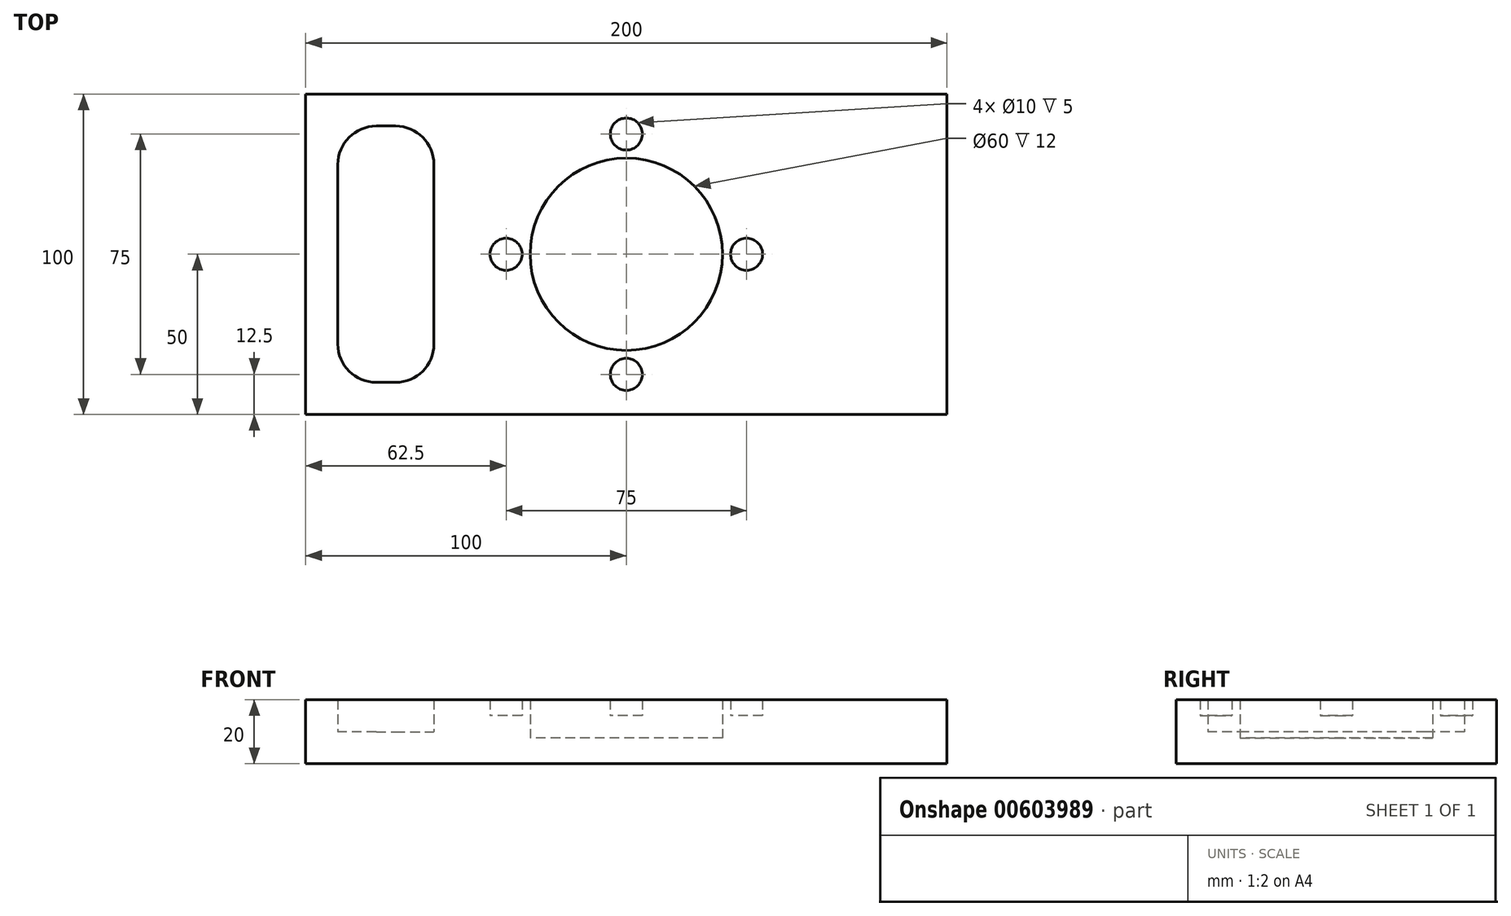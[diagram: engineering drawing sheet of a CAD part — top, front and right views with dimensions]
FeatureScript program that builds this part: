
annotation { "Feature Type Name" : "Feature", "Feature Type Description" : "" }
export const myFeature = defineFeature(function(context is Context, id is Id, definition is map)
    precondition{}
    {
        {
            var Q0;
            Q0=qCreatedBy(makeId("Top.planeOp"),FACE);
            var sketch = newSketch(context, id + "F0", { "sketchPlane" : qUnion([Q0])});
            skLineSegment(sketch, "E0.bottom", {"start": v(-100, 50) * mm, "end": v(100, 50) * mm});
            skLineSegment(sketch, "E0.top", {"start": v(-100, -50) * mm, "end": v(100, -50) * mm});
            skLineSegment(sketch, "E0.left", {"start": v(-100, 50) * mm, "end": v(-100, -50) * mm});
            skLineSegment(sketch, "E0.right", {"start": v(100, 50) * mm, "end": v(100, -50) * mm});
            skPoint(sketch, "E0.middle", {"position": v(0, 0) * mm});
            skSolve(sketch);
        }
        {
            var Q0;
            Q0=makeQuery(id+"F0.imprint","IMPRINT",FACE,{"disambiguationData":[TD([[makeQuery(id+"F0.imprint","IMPRINT",EDGE,{"derivedFrom":sQuery(id+"F0.wireOp",EDGE,"E0.bottom")}),-1.0]])]});
            extrude(context, id + "F1", {"entities" : qUnion([Q0]), "depth" : 8 * mm, "offsetDistance" : 25 * mm});
        }
        {
            var Q0;
            Q0=makeQuery(id+"F1.opExtrude","CAP_FACE",FACE,{"disambiguationData":[OSD([sQuery(id+"F0.wireOp",EDGE,"E0.bottom"),sQuery(id+"F0.wireOp",EDGE,"E0.top"),sQuery(id+"F0.wireOp",EDGE,"E0.left"),sQuery(id+"F0.wireOp",EDGE,"E0.right")])],"isStart":false});
            var sketch = newSketch(context, id + "F2", { "sketchPlane" : qUnion([Q0])});
            skLineSegment(sketch, "E1.bottom", {"start": v(-100, 50) * mm, "end": v(100, 50) * mm});
            skLineSegment(sketch, "E1.top", {"start": v(-100, -50) * mm, "end": v(100, -50) * mm});
            skLineSegment(sketch, "E1.left", {"start": v(-100, 50) * mm, "end": v(-100, -50) * mm});
            skLineSegment(sketch, "E1.right", {"start": v(100, 50) * mm, "end": v(100, -50) * mm});
            skPoint(sketch, "E1.middle", {"position": v(0, 0) * mm});
            skCircle(sketch, "E2", {"center": v(0, 0) * mm, "radius": 30 * mm});
            skSolve(sketch);
        }
        {
            var Q0;
            Q0=makeQuery(id+"F2.imprint","IMPRINT",FACE,{"disambiguationData":[TD([[makeQuery(id+"F2.imprint","IMPRINT",EDGE,{"derivedFrom":sQuery(id+"F2.wireOp",EDGE,"E1.bottom")}),-1.0]])]});
            extrude(context, id + "F3", {"entities" : qUnion([Q0]), "operationType" : NewBodyOperationType.ADD, "depth" : 2 * mm, "offsetDistance" : 25 * mm});
        }
        {
            var Q0;
            Q0=makeQuery(id+"F3.opExtrude","CAP_FACE",FACE,{"disambiguationData":[OSD([sQuery(id+"F2.wireOp",EDGE,"E1.bottom"),sQuery(id+"F2.wireOp",EDGE,"E1.top"),sQuery(id+"F2.wireOp",EDGE,"E1.left"),sQuery(id+"F2.wireOp",EDGE,"E1.right"),sQuery(id+"F2.wireOp",EDGE,"E2")])],"isStart":false});
            var sketch = newSketch(context, id + "F4", { "sketchPlane" : qUnion([Q0])});
            skLineSegment(sketch, "E3.bottom", {"start": v(-78, 40) * mm, "end": v(-72, 40) * mm});
            skLineSegment(sketch, "E3.top", {"start": v(-78, -40) * mm, "end": v(-72, -40) * mm});
            skLineSegment(sketch, "E3.left", {"start": v(-90, 28) * mm, "end": v(-90, -28) * mm});
            skLineSegment(sketch, "E3.right", {"start": v(-60, 28) * mm, "end": v(-60, -28) * mm});
            skPoint(sketch, "E3.middle", {"position": v(-75, 0) * mm});
            skPoint(sketch, "E4.visualSharp", {"position": v(-90, 40) * mm});
            skArc(sketch, "E4.filletArc", {"start": v(-78, 40) * mm, "mid": v(-86.49, 36.49) * mm, "end": v(-90, 28) * mm});
            skPoint(sketch, "E5.visualSharp", {"position": v(-60, 40) * mm});
            skArc(sketch, "E5.filletArc", {"start": v(-60, 28) * mm, "mid": v(-63.51, 36.49) * mm, "end": v(-72, 40) * mm});
            skPoint(sketch, "E6.visualSharp", {"position": v(-90, -40) * mm});
            skArc(sketch, "E6.filletArc", {"start": v(-90, -28) * mm, "mid": v(-86.49, -36.49) * mm, "end": v(-78, -40) * mm});
            skPoint(sketch, "E7.visualSharp", {"position": v(-60, -40) * mm});
            skArc(sketch, "E7.filletArc", {"start": v(-72, -40) * mm, "mid": v(-63.51, -36.49) * mm, "end": v(-60, -28) * mm});
            skCircle(sketch, "E8", {"center": v(0, 0) * mm, "radius": 30 * mm});
            skSolve(sketch);
        }
        {
            var Q0;
            Q0=makeQuery(id+"F4.imprint","IMPRINT",FACE,{"disambiguationData":[TD([[makeQuery(id+"F4.imprint","IMPRINT",EDGE,{"derivedFrom":sQuery(id+"F4.wireOp",EDGE,"E3.bottom")}),1.0]])]});
            extrude(context, id + "F5", {"entities" : qUnion([Q0]), "operationType" : NewBodyOperationType.ADD, "depth" : 5 * mm, "offsetDistance" : 25 * mm});
        }
        {
            var Q0;
            Q0=makeQuery(id+"F5.opExtrude","CAP_FACE",FACE,{"disambiguationData":[OSD([sQuery(id+"F2.wireOp",EDGE,"E1.bottom"),sQuery(id+"F2.wireOp",EDGE,"E1.top"),sQuery(id+"F2.wireOp",EDGE,"E1.left"),sQuery(id+"F2.wireOp",EDGE,"E1.right"),sQuery(id+"F4.wireOp",EDGE,"E3.bottom"),sQuery(id+"F4.wireOp",EDGE,"E3.top"),sQuery(id+"F4.wireOp",EDGE,"E3.left"),sQuery(id+"F4.wireOp",EDGE,"E3.right"),sQuery(id+"F4.wireOp",EDGE,"E4.filletArc"),sQuery(id+"F4.wireOp",EDGE,"E5.filletArc"),sQuery(id+"F4.wireOp",EDGE,"E6.filletArc"),sQuery(id+"F4.wireOp",EDGE,"E7.filletArc"),sQuery(id+"F4.wireOp",EDGE,"E8")])],"isStart":false});
            var sketch = newSketch(context, id + "F6", { "sketchPlane" : qUnion([Q0])});
            skLineSegment(sketch, "E9.bottom", {"start": v(-78, 40) * mm, "end": v(-72, 40) * mm});
            skLineSegment(sketch, "E9.top", {"start": v(-78, -40) * mm, "end": v(-72, -40) * mm});
            skLineSegment(sketch, "E9.left", {"start": v(-90, 28) * mm, "end": v(-90, -28) * mm});
            skLineSegment(sketch, "E9.right", {"start": v(-60, 28) * mm, "end": v(-60, -28) * mm});
            skPoint(sketch, "E9.middle", {"position": v(-75, 0) * mm});
            skPoint(sketch, "E10.visualSharp", {"position": v(-90, 40) * mm});
            skArc(sketch, "E10.filletArc", {"start": v(-78, 40) * mm, "mid": v(-86.49, 36.49) * mm, "end": v(-90, 28) * mm});
            skPoint(sketch, "E11.visualSharp", {"position": v(-60, 40) * mm});
            skArc(sketch, "E11.filletArc", {"start": v(-60, 28) * mm, "mid": v(-63.51, 36.49) * mm, "end": v(-72, 40) * mm});
            skPoint(sketch, "E12.visualSharp", {"position": v(-90, -40) * mm});
            skArc(sketch, "E12.filletArc", {"start": v(-90, -28) * mm, "mid": v(-86.49, -36.49) * mm, "end": v(-78, -40) * mm});
            skPoint(sketch, "E13.visualSharp", {"position": v(-60, -40) * mm});
            skArc(sketch, "E13.filletArc", {"start": v(-72, -40) * mm, "mid": v(-63.51, -36.49) * mm, "end": v(-60, -28) * mm});
            skCircle(sketch, "E14", {"center": v(0, 0) * mm, "radius": 30 * mm});
            skCircle(sketch, "E15", {"center": v(0, 0) * mm, "radius": 45 * mm});
            skCircle(sketch, "E16", {"center": v(0, 0) * mm, "radius": 37.5 * mm, "construction": true});
            skCircle(sketch, "E17", {"center": v(0, 37.5) * mm, "radius": 5 * mm});
            skCircle(sketch, "E18", {"center": v(37.5, 0) * mm, "radius": 5 * mm});
            skCircle(sketch, "E19", {"center": v(0, -37.5) * mm, "radius": 5 * mm});
            skCircle(sketch, "E20", {"center": v(-37.5, 0) * mm, "radius": 5 * mm});
            skSolve(sketch);
        }
        {
            var Q0;
            Q0=makeQuery(id+"F6.imprint","IMPRINT",FACE,{"disambiguationData":[TD([[makeQuery(id+"F6.imprint","IMPRINT",EDGE,{"derivedFrom":sQuery(id+"F6.wireOp",EDGE,"E14")}),-1.0]])]});
            extrude(context, id + "F7", {"entities" : qUnion([Q0]), "operationType" : NewBodyOperationType.ADD, "depth" : 5 * mm, "offsetDistance" : 25 * mm});
        }
        {
            var Q0;
            {var subQ0=sQuery(id+"F4.wireOp",EDGE,"E3.top");var subQ1=sQuery(id+"F4.wireOp",EDGE,"E3.bottom");var subQ2=sQuery(id+"F2.wireOp",EDGE,"E1.right");var subQ3=sQuery(id+"F2.wireOp",EDGE,"E1.left");var subQ4=sQuery(id+"F2.wireOp",EDGE,"E1.top");var subQ5=sQuery(id+"F2.wireOp",EDGE,"E1.bottom");var subQ6=sQuery(id+"F4.wireOp",EDGE,"E3.left");var subQ7=sQuery(id+"F4.wireOp",EDGE,"E3.right");var subQ8=sQuery(id+"F4.wireOp",EDGE,"E4.filletArc");var subQ9=sQuery(id+"F4.wireOp",EDGE,"E5.filletArc");var subQ10=sQuery(id+"F4.wireOp",EDGE,"E6.filletArc");var subQ11=sQuery(id+"F4.wireOp",EDGE,"E7.filletArc");Q0=makeQuery(id+"F7.boolean.opBoolean","SPLIT",FACE,{"disambiguationData":[TD([makeQuery(id+"F1.opExtrude","SWEPT_FACE",FACE,{"disambiguationData":[OSD([sQuery(id+"F0.wireOp",EDGE,"E0.bottom")])]})])],"derivedFrom":makeQuery(id+"F5.opExtrude","CAP_FACE",FACE,{"disambiguationData":[OSD([subQ5,subQ4,subQ3,subQ2,subQ1,subQ0,subQ6,subQ7,subQ8,subQ9,subQ10,subQ11,sQuery(id+"F4.wireOp",EDGE,"E8")])],"isStart":false})});}
            extrude(context, id + "F8", {"entities" : qUnion([Q0]), "operationType" : NewBodyOperationType.ADD, "depth" : 5 * mm, "offsetDistance" : 25 * mm});
        }
    });
